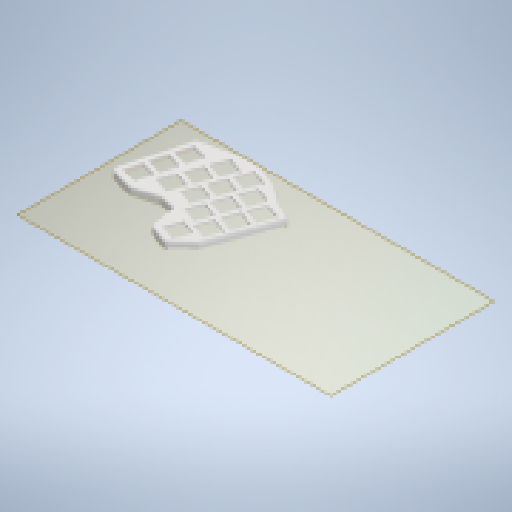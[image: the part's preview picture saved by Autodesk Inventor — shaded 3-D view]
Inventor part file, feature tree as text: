
AUTODESK INVENTOR PART (.ipt)
format: ipt  version: 2024 (Build 280153000, 153)  size: 762,368 bytes
history: native  units: mm
features: reference x49, extrude x5, sketch x5, other x4, plane x3, projected_geometry x2, fillet x1
ambient origin geometry x8: Origin, YZ Plane, XZ Plane, XY Plane, X Axis, Y Axis, Z Axis, Center Point
bodies: Volumenkörper1 (feature_tree)
feature tree (69):
  plane  "Arbeitsebene1"
  extrude  "Extrusion1"  Depth=2.0mm
  extrude  "Extrusion2"  Depth=2.0mm
  fillet  "Rundung1"  Radius=2.0mm
  sketch  "Skizze3"  dims[d17=2.0mm d18=2.0mm]
  plane  "Arbeitsebene2"
  extrude  "Extrusion3"  Depth=2.0mm
  extrude  "Extrusion4"  Depth=2.0mm
  sketch  "Skizze5"  dims[d22=2.0mm d23=2.0mm d24=2.0mm d25=3.5mm d26=0.0mm d27=1.5mm d28=0.0mm d29=2.0mm d30=2.0mm d31=0.0mm d32=15.0mm d33=15.0mm d34=15.0mm d35=15.0mm d36=30.0mm d38=19.0mm d39=10.0mm d41=10.0mm d43=15.0mm d44=15.0mm d45=30.0mm d47=19.0mm d48=10.0mm d50=10.0mm d52=15.0mm d53=15.0mm d54=30.0mm d56=19.0mm d57=10.0mm d59=10.0mm d61=15.0mm d62=15.0mm d63=30.0mm d65=19.0mm d66=10.0mm d68=10.0mm d70=15.0mm d71=15.0mm d72=30.0mm d74=19.0mm d75=10.0mm d77=10.0mm d79=2.0mm d80=0.0mm d81=5.0mm d82=5.0mm d83=5.0mm d84=2.9mm d85=2.9mm d86=2.9mm d87=2.0mm d88=0.0mm]
  plane  "Arbeitsebene3"
  extrude  "Extrusion5"  Depth=10.0mm
  sketch  "Skizze1"  dims[d12=2.0mm d13=2.0mm]
  reference  "Referenz1"
  reference  "Referenz2"
  reference  "Referenz3"
  reference  "Referenz4"
  reference  "Referenz5"
  reference  "Referenz6"
  reference  "Referenz7"
  reference  "Referenz8"
  reference  "Referenz9"
  reference  "Referenz10"
  reference  "Referenz11"
  reference  "Referenz12"
  reference  "Referenz13"
  reference  "Referenz14"
  reference  "Referenz15"
  reference  "Referenz16"
  reference  "Referenz17"
  reference  "Referenz18"
  reference  "Referenz19"
  reference  "Referenz20"
  reference  "Referenz21"
  reference  "Referenz22"
  reference  "Referenz23"
  sketch  "Skizze2"  dims[d14=2.0mm d15=2.0mm d16=2.0mm]
  projected_geometry  "Projizierte Kontur1"
  projected_geometry  "Projizierte Kontur2"
  reference  "Referenz24"
  reference  "Referenz25"
  reference  "Referenz26"
  reference  "Referenz27"
  reference  "Referenz28"
  sketch  "Skizze4"  dims[d19=2.0mm d20=2.0mm]
  reference  "Referenz29"
  reference  "Referenz30"
  reference  "Referenz31"
  reference  "Referenz32"
  reference  "Referenz33"
  reference  "Referenz34"
  reference  "Referenz35"
  reference  "Referenz36"
  reference  "Referenz37"
  reference  "Referenz38"
  reference  "Referenz39"
  reference  "Referenz40"
  reference  "Referenz41"
  reference  "Referenz42"
  reference  "Referenz43"
  reference  "Referenz44"
  reference  "Referenz45"
  reference  "Referenz46"
  reference  "Referenz47"
  reference  "Referenz48"
  reference  "Referenz49"
  other  "<userpath>\OneDrive\Keyboards\Blavinge\case\case.iam"
  other  "case.iam"
  other  "blavinge:1"
  other  "middle_top:1"
